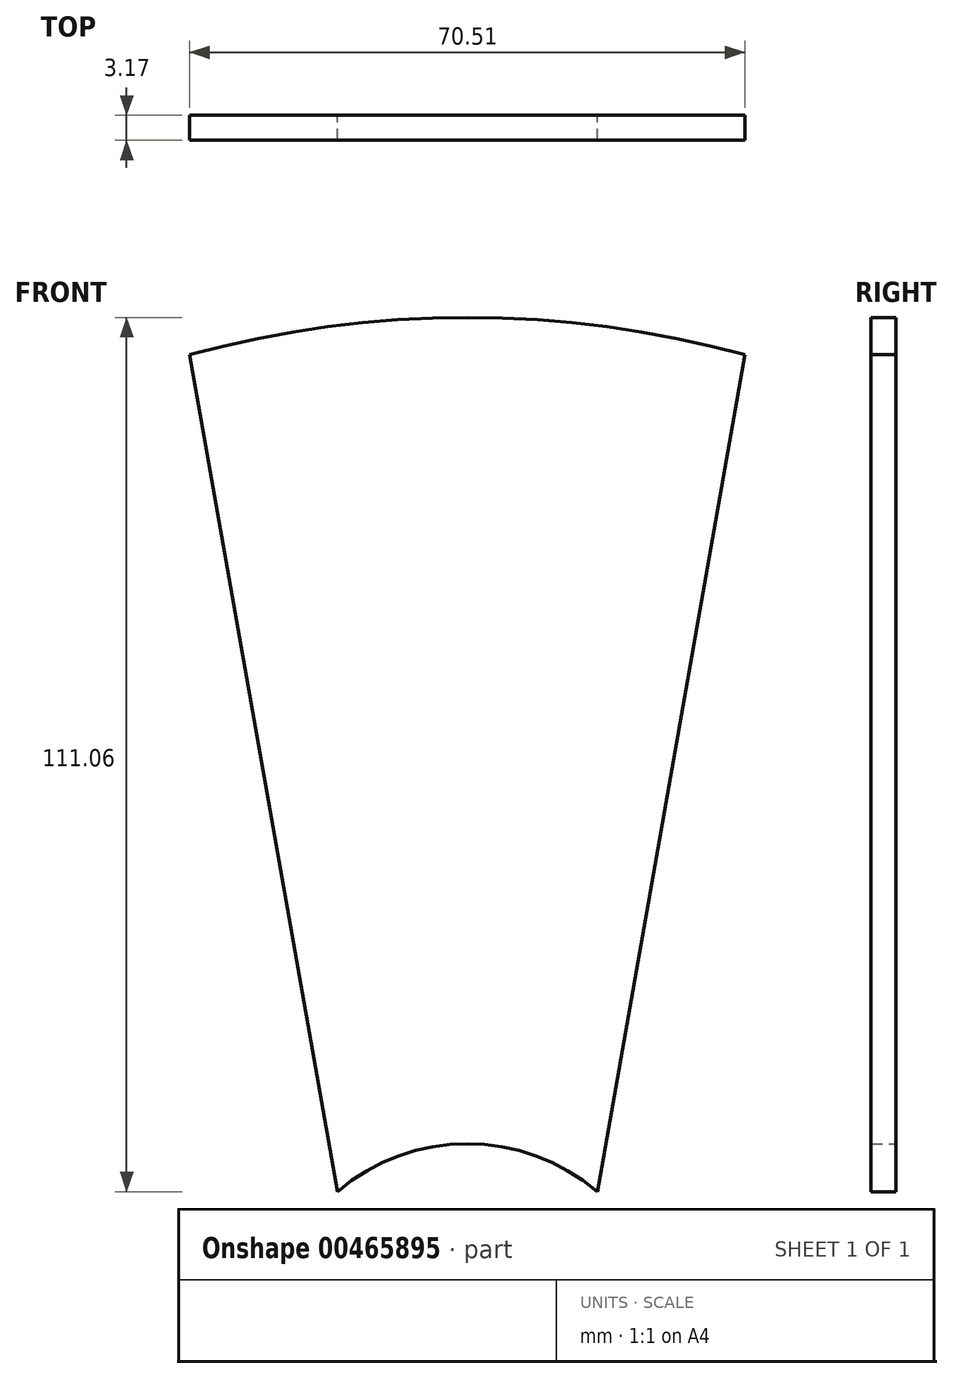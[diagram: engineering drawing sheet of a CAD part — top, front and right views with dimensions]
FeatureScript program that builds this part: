
annotation { "Feature Type Name" : "Feature", "Feature Type Description" : "" }
export const myFeature = defineFeature(function(context is Context, id is Id, definition is map)
    precondition{}
    {
        {
            var Q0;
            Q0=qCreatedBy(makeId("Front.planeOp"),FACE);
            var sketch = newSketch(context, id + "F0", { "sketchPlane" : qUnion([Q0])});
            skLineSegment(sketch, "E0", {"start": v(19.12, 38) * mm, "end": v(0.38, -68.32) * mm});
            skLineSegment(sketch, "E1", {"start": v(0.38, -68.32) * mm, "end": v(-32.64, -68.32) * mm});
            skLineSegment(sketch, "E2", {"start": v(-32.64, -68.32) * mm, "end": v(-51.39, 38) * mm});
            skArc(sketch, "E3", {"start": v(19.12, 38) * mm, "mid": v(-16.13, 42.74) * mm, "end": v(-51.39, 38) * mm});
            skArc(sketch, "E4", {"start": v(0.38, -68.32) * mm, "mid": v(-16.13, -62.22) * mm, "end": v(-32.64, -68.32) * mm});
            skSolve(sketch);
        }
        {
            var Q0;
            Q0=makeQuery(id+"F0.imprint","IMPRINT",FACE,{"disambiguationData":[TD([[makeQuery(id+"F0.imprint","IMPRINT",EDGE,{"derivedFrom":sQuery(id+"F0.wireOp",EDGE,"E0")}),-1.0]])]});
            extrude(context, id + "F1", {"entities" : qUnion([Q0]), "depth" : 3.17 * mm});
        }
    });
